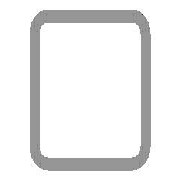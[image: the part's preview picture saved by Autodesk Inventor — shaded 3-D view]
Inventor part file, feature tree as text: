
AUTODESK INVENTOR PART (.ipt)
format: ipt  version: 2025 (Build 290162010, 162A)  size: 150,016 bytes
history: native  units: mm (DEFAULTED — no unit token found)
features: other x4, plane x3, split x2, sketch x1
ambient origin geometry x8: Origin, YZ Plane, XZ Plane, XY Plane, X Axis, Y Axis, Z Axis, Center Point
bodies: Solid1 (feature_tree), Body (feature_tree)
feature tree (10):
  parser-record x1  (decoder bookkeeping rows leaked as tree rows — omitted from the tree; the rows remain in map.json)
  other  "Driven Length"
  other  "Start Plane"
  other  "End Plane"
  plane  "Work Plane4"
  split  "Split1"
  plane  "Work Plane5"
  split  "Split2"
  sketch  "Sketch3"  dims[d3=3056.510663mm d4=0.0mm d7=6.0mm d9=80.0mm d11=80.0mm d12=3.0mm d13=70.868598mm d14=3127.379261mm d15=40.0mm d16=40.0mm d17=90.0deg d18=3056.510663mm]
  plane  "Work Plane3"
